# Revit family: 71786XXX_NEW
name_source: partatom
category: Plumbing Fixtures
revit_build: Autodesk Revit 2018 (Build: 20170223_1515(x64)
units: mm (PartAtom-declared; Revit-internal decimal feet)

## family parameters
Always vertical = No
Cut with Voids When Loaded = No
OmniClass Number = 23.45.00.00
OmniClass Title = Sanitary, Laundry, and Cleaning Equipment
Part Type = Normal
Room Calculation Point = No
Round Connector Dimension = Use Diameter
Shared = No
Work Plane-Based = Yes

## types (6) — shared parameters
Always visible = Yes
BIMobject category = Sanitary Taps & Mixers
Default Elevation = 1219.2 mm  [stored 4 ft]
Design country = Germany
EAN code = 4059625334140
Edition number = 1
GTIN code = https://4059625334140
IFC Classification = Sanitary Terminal
Installation instructions = https://www.hansgrohe.com
Manufacturer country = Germany
Manufacturer name = hansgrohe
Masterformat 2014 Code = 41 14 33
Masterformat 2014 Description = Mixers
Material secondary = Chrome
NBS Reference Code = 35-06-82
NBS Reference Description = Shower Mixers
Product Guid = ed296ed9-becb-4aa4-abae-2400662893d8
Product SKU = 71786XXX
Product data url = https://www.bimobject.com
Product family = Talis E
Product group = Basin mixers
Product name = 71786XXX Talis E Single lever basin mixer 110 with pop-up waste set Finland
Product url = https://www.hansgrohe.com
QR code = https://www.bimobject.com
Technical description = https://www.hansgrohe.com
Uniclass 2.0 Code = PR-35-06-82
Uniclass 2.0 Description = Shower Mixers
Uniclass 2015 Code = Pr_60_75_08_54
Uniclass 2015 Name = Mixers
Weight Net (Kg) = 1,9

## per-type parameters (varying)
| type | Material 1 |
| 990 Polished Gold Optic | Hansgrohe - Metal - 990 Polished Gold Optic |
| 340 Brushed Black Chrome | Hansgrohe - Metal - 340 Brushed Black Chrome |
| 140 Brushed Bronze | Hansgrohe - Metal - 140 Brushed Bronze |
| 700 Matt White | Hansgrohe - Metal - 700 Matt White |
| 670 Matte Black | Hansgrohe - Metal - 670 Matte Black |
| 000 Chrome | Hansgrohe - Metal - 000 Chrome |

note: [stored X ft] marks values corroborated as IEEE doubles in the binary element streams (Revit-internal decimal feet)

## geometry (parser evidence)
native form markers: Sweep x1
no freeform markers — native parametric forms only
